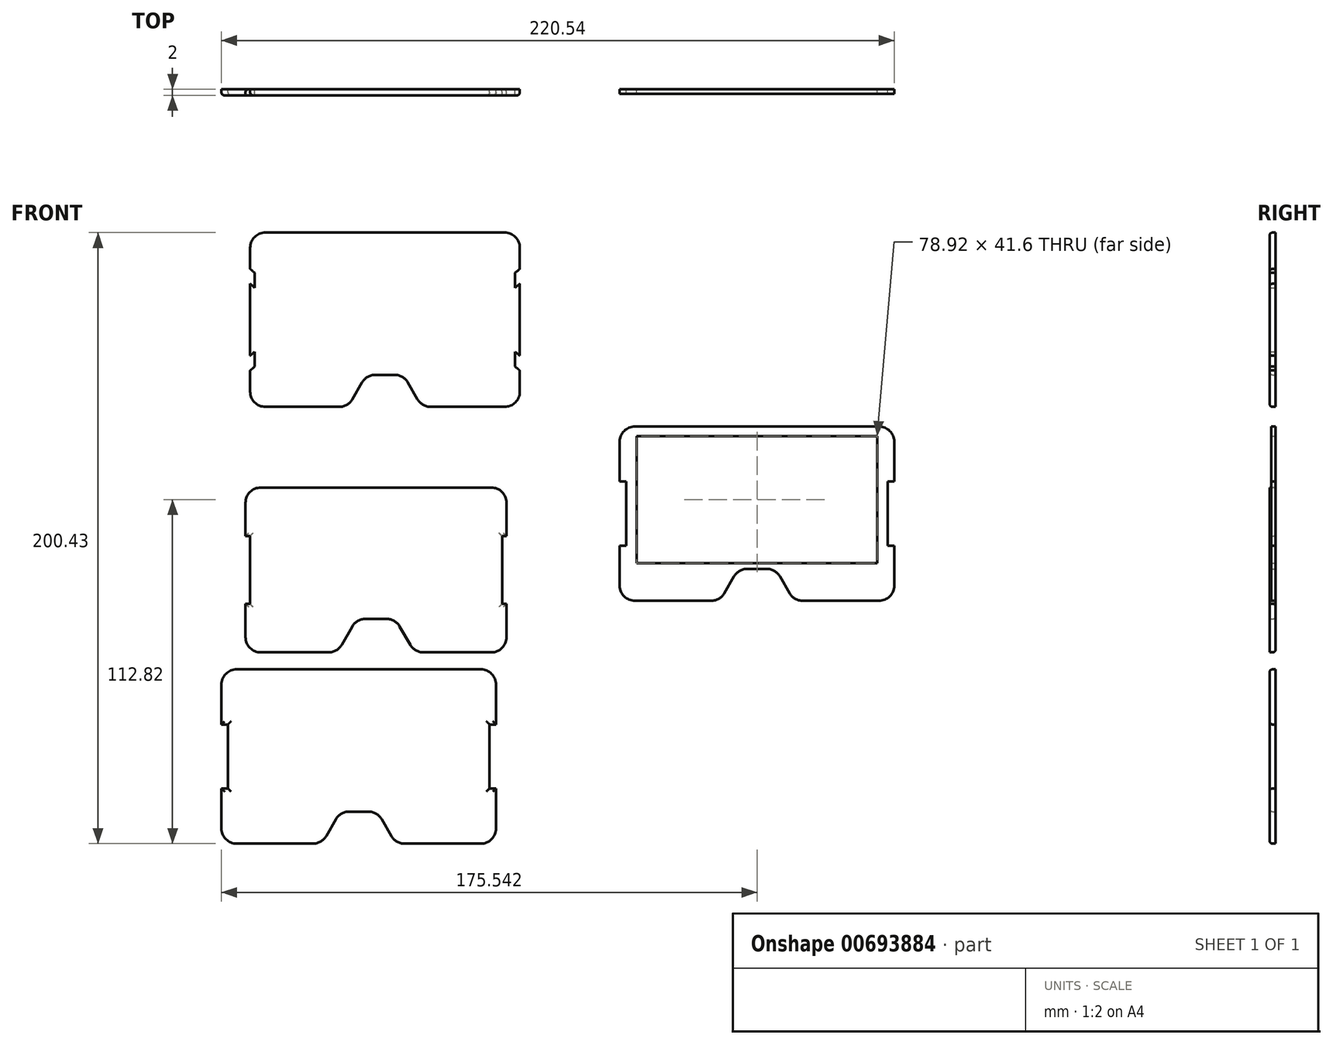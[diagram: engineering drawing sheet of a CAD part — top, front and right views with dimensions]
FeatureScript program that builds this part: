
annotation { "Feature Type Name" : "Feature", "Feature Type Description" : "" }
export const myFeature = defineFeature(function(context is Context, id is Id, definition is map)
    precondition{}
    {
        {
            var Q0;
            Q0=qCreatedBy(makeId("Front.planeOp"),FACE);
            var sketch = newSketch(context, id + "F0", { "sketchPlane" : qUnion([Q0])});
            skPoint(sketch, "E0.middle", {"position": v(0, 0) * mm});
            skPoint(sketch, "E1.visualSharp", {"position": v(43.77, 28.02) * mm});
            skArc(sketch, "E1.filletArc", {"start": v(42.78, 22.03) * mm, "mid": v(41.32, 25.56) * mm, "end": v(37.78, 27.03) * mm});
            skPoint(sketch, "E2.visualSharp", {"position": v(-42.78, 27.03) * mm});
            skArc(sketch, "E2.filletArc", {"start": v(-37.78, 27.03) * mm, "mid": v(-41.32, 25.56) * mm, "end": v(-42.78, 22.03) * mm});
            skPoint(sketch, "E3.visualSharp", {"position": v(-43.77, -28.02) * mm});
            skArc(sketch, "E3.filletArc", {"start": v(-42.78, -22.03) * mm, "mid": v(-41.32, -25.56) * mm, "end": v(-37.78, -27.03) * mm});
            skPoint(sketch, "E4.visualSharp", {"position": v(42.78, -27.03) * mm});
            skArc(sketch, "E4.filletArc", {"start": v(37.78, -27.03) * mm, "mid": v(41.32, -25.56) * mm, "end": v(42.78, -22.03) * mm});
            skLineSegment(sketch, "E5", {"start": v(42.78, 0) * mm, "end": v(0, 0) * mm, "construction": true});
            skLineSegment(sketch, "E6", {"start": v(0, 0) * mm, "end": v(0, 27.03) * mm, "construction": true});
            skLineSegment(sketch, "E7", {"start": v(42.78, 13.02) * mm, "end": v(42.78, 22.03) * mm});
            skLineSegment(sketch, "E8.2", {"start": v(-11.23, -24.53) * mm, "end": v(-7.78, -18.55) * mm});
            skLineSegment(sketch, "E8.3", {"start": v(-3.45, -16.05) * mm, "end": v(3.45, -16.05) * mm});
            skLineSegment(sketch, "E8.4", {"start": v(7.78, -18.55) * mm, "end": v(11.23, -24.53) * mm});
            skPoint(sketch, "E8.0.midPoint", {"position": v(0, -38) * mm});
            skLineSegment(sketch, "E9", {"start": v(37.78, -27.03) * mm, "end": v(15.56, -27.03) * mm});
            skLineSegment(sketch, "E10", {"start": v(-15.56, -27.03) * mm, "end": v(-37.78, -27.03) * mm});
            skLineSegment(sketch, "E11", {"start": v(-37.78, 27.03) * mm, "end": v(37.78, 27.03) * mm});
            skPoint(sketch, "E12.visualSharp", {"position": v(12.67, -27.03) * mm});
            skArc(sketch, "E12.filletArc", {"start": v(11.23, -24.53) * mm, "mid": v(13.06, -26.36) * mm, "end": v(15.56, -27.03) * mm});
            skPoint(sketch, "E13.visualSharp", {"position": v(6.34, -16.05) * mm});
            skArc(sketch, "E13.filletArc", {"start": v(7.78, -18.55) * mm, "mid": v(5.95, -16.72) * mm, "end": v(3.45, -16.05) * mm});
            skPoint(sketch, "E14.visualSharp", {"position": v(-6.34, -16.05) * mm});
            skArc(sketch, "E14.filletArc", {"start": v(-3.45, -16.05) * mm, "mid": v(-5.95, -16.72) * mm, "end": v(-7.78, -18.55) * mm});
            skPoint(sketch, "E15.visualSharp", {"position": v(-12.67, -27.03) * mm});
            skArc(sketch, "E15.filletArc", {"start": v(-15.56, -27.03) * mm, "mid": v(-13.06, -26.36) * mm, "end": v(-11.23, -24.53) * mm});
            skLineSegment(sketch, "E16", {"start": v(41.35, 0) * mm, "end": v(41.35, 11.08) * mm});
            skLineSegment(sketch, "E17", {"start": v(41.35, 11.08) * mm, "end": v(42.78, 11.08) * mm});
            skLineSegment(sketch, "E18", {"start": v(42.78, 11.08) * mm, "end": v(42.78, 13.02) * mm});
            skLineSegment(sketch, "E19.MirrorCS", {"start": v(41.35, 0) * mm, "end": v(41.35, -11.08) * mm});
            skLineSegment(sketch, "E20.MirrorCS", {"start": v(41.35, -11.08) * mm, "end": v(42.78, -11.08) * mm});
            skLineSegment(sketch, "E21", {"start": v(42.78, -11.08) * mm, "end": v(42.78, -22.03) * mm});
            skLineSegment(sketch, "E22.MirrorCS", {"start": v(-41.35, 0) * mm, "end": v(-41.35, -11.08) * mm});
            skLineSegment(sketch, "E23.MirrorCS", {"start": v(-41.35, -11.08) * mm, "end": v(-42.78, -11.08) * mm});
            skLineSegment(sketch, "E24.MirrorCS", {"start": v(-41.35, 11.08) * mm, "end": v(-42.78, 11.08) * mm});
            skLineSegment(sketch, "E25.MirrorCS", {"start": v(-41.35, 0) * mm, "end": v(-41.35, 11.08) * mm});
            skLineSegment(sketch, "E26", {"start": v(-42.78, 22.03) * mm, "end": v(-42.78, 11.08) * mm});
            skLineSegment(sketch, "E27", {"start": v(-42.78, -22.03) * mm, "end": v(-42.78, -11.08) * mm});
            skSolve(sketch);
        }
        {
            var Q0;
            Q0=makeQuery(id+"F0.imprint","IMPRINT",FACE,{"disambiguationData":[TD([[makeQuery(id+"F0.imprint","IMPRINT",EDGE,{"derivedFrom":sQuery(id+"F0.wireOp",EDGE,"E1.filletArc")}),1.0]])]});
            extrude(context, id + "F1", {"entities" : qUnion([Q0]), "depth" : 2 * mm, "offsetDistance" : 25 * mm});
        }
        {
            var Q0;
            Q0=makeQuery(id+"F1.opExtrude","CAP_FACE",FACE,{"disambiguationData":[OSD([sQuery(id+"F0.wireOp",EDGE,"E1.filletArc"),sQuery(id+"F0.wireOp",EDGE,"E2.filletArc"),sQuery(id+"F0.wireOp",EDGE,"E3.filletArc"),sQuery(id+"F0.wireOp",EDGE,"E4.filletArc"),sQuery(id+"F0.wireOp",EDGE,"swWxlsA6-b0p4-RpLw-KjBK-F9TTlwRh0JCC.bottom"),sQuery(id+"F0.wireOp",EDGE,"swWxlsA6-b0p4-RpLw-KjBK-F9TTlwRh0JCC.top"),sQuery(id+"F0.wireOp",EDGE,"swWxlsA6-b0p4-RpLw-KjBK-F9TTlwRh0JCC.right"),sQuery(id+"F0.wireOp",EDGE,"38b65e96-5360-40c4-b25c-9e81677ce4790.MirrorCS"),sQuery(id+"F0.wireOp",EDGE,"38b65e96-5360-40c4-b25c-9e81677ce4791.MirrorCS"),sQuery(id+"F0.wireOp",EDGE,"38b65e96-5360-40c4-b25c-9e81677ce4792.MirrorCS"),sQuery(id+"F0.wireOp",EDGE,"1M21Hp1W-tZvE-ZjFn-AURu-wiaH579pFp8t"),sQuery(id+"F0.wireOp",EDGE,"E7"),sQuery(id+"F0.wireOp",EDGE,"a8fVo7L8-jyON-3xXB-mA3J-mLnhyzgucnCO"),sQuery(id+"F0.wireOp",EDGE,"VKjqsVk1-CC2T-ZNqS-4vh9-m0KNvKaINnyJ"),sQuery(id+"F0.wireOp",EDGE,"E8.2"),sQuery(id+"F0.wireOp",EDGE,"E8.3"),sQuery(id+"F0.wireOp",EDGE,"E8.4"),sQuery(id+"F0.wireOp",EDGE,"E9"),sQuery(id+"F0.wireOp",EDGE,"E10"),sQuery(id+"F0.wireOp",EDGE,"E11"),sQuery(id+"F0.wireOp",EDGE,"E12.filletArc"),sQuery(id+"F0.wireOp",EDGE,"E13.filletArc"),sQuery(id+"F0.wireOp",EDGE,"E14.filletArc"),sQuery(id+"F0.wireOp",EDGE,"E15.filletArc")])],"isStart":true});
            fillet(context, id + "F2", {"entities" : qUnion([Q0]), "radius" : 1 * mm, "tangentPropagation" : true, "allowEdgeOverflow" : false});
        }
        {
            var Q0;
            Q0=qCreatedBy(makeId("Front.planeOp"),FACE);
            var sketch = newSketch(context, id + "F3", { "sketchPlane" : qUnion([Q0])});
            skLineSegment(sketch, "E28.bottom", {"start": v(-45.66, -32.6) * mm, "end": v(34.34, -32.6) * mm});
            skLineSegment(sketch, "E29", {"start": v(-5.66, -32.6) * mm, "end": v(-5.66, -89.77) * mm, "construction": true});
            skPoint(sketch, "E30.middle", {"position": v(-5.66, -61.18) * mm});
            skLineSegment(sketch, "E31", {"start": v(-48.54, -61.18) * mm, "end": v(-48.54, -71.68) * mm});
            skLineSegment(sketch, "E32.MirrorCS", {"start": v(-48.54, -61.18) * mm, "end": v(-48.54, -50.68) * mm});
            skLineSegment(sketch, "E33", {"start": v(-48.54, -50.68) * mm, "end": v(-50.66, -50.68) * mm});
            skLineSegment(sketch, "E34", {"start": v(-48.54, -71.68) * mm, "end": v(-50.66, -71.68) * mm});
            skLineSegment(sketch, "E35", {"start": v(-50.66, -84.77) * mm, "end": v(-50.66, -71.68) * mm});
            skLineSegment(sketch, "E36", {"start": v(-50.66, -50.68) * mm, "end": v(-50.66, -37.6) * mm});
            skLineSegment(sketch, "E37", {"start": v(-5.66, -61.18) * mm, "end": v(-48.54, -61.18) * mm, "construction": true});
            skLineSegment(sketch, "E38.MirrorCS", {"start": v(37.22, -71.68) * mm, "end": v(39.34, -71.68) * mm});
            skLineSegment(sketch, "E39.MirrorCS", {"start": v(37.22, -61.18) * mm, "end": v(37.22, -71.68) * mm});
            skLineSegment(sketch, "E40.MirrorCS", {"start": v(37.22, -61.18) * mm, "end": v(37.22, -50.68) * mm});
            skLineSegment(sketch, "E41.MirrorCS", {"start": v(37.22, -50.68) * mm, "end": v(39.34, -50.68) * mm});
            skLineSegment(sketch, "E42", {"start": v(39.34, -37.6) * mm, "end": v(39.34, -50.68) * mm});
            skLineSegment(sketch, "E43", {"start": v(39.34, -71.68) * mm, "end": v(39.34, -84.77) * mm});
            skLineSegment(sketch, "E44.0", {"start": v(-8.84, -79.26) * mm, "end": v(-2.48, -79.26) * mm});
            skLineSegment(sketch, "E44.1", {"start": v(1.85, -81.76) * mm, "end": v(5.02, -87.27) * mm});
            skLineSegment(sketch, "E44.5", {"start": v(-16.34, -87.27) * mm, "end": v(-13.17, -81.76) * mm});
            skPoint(sketch, "E44.0.midPoint", {"position": v(-5.66, -79.26) * mm});
            skLineSegment(sketch, "E45", {"start": v(-45.66, -89.77) * mm, "end": v(-20.67, -89.77) * mm});
            skLineSegment(sketch, "E46", {"start": v(9.35, -89.77) * mm, "end": v(34.34, -89.77) * mm});
            skPoint(sketch, "E47.visualSharp", {"position": v(-50.66, -32.6) * mm});
            skArc(sketch, "E47.filletArc", {"start": v(-45.66, -32.6) * mm, "mid": v(-49.2, -34.06) * mm, "end": v(-50.66, -37.6) * mm});
            skPoint(sketch, "E48.visualSharp", {"position": v(39.34, -32.6) * mm});
            skArc(sketch, "E48.filletArc", {"start": v(39.34, -37.6) * mm, "mid": v(37.88, -34.06) * mm, "end": v(34.34, -32.6) * mm});
            skPoint(sketch, "E49.visualSharp", {"position": v(39.34, -89.77) * mm});
            skArc(sketch, "E49.filletArc", {"start": v(34.34, -89.77) * mm, "mid": v(37.88, -88.3) * mm, "end": v(39.34, -84.77) * mm});
            skPoint(sketch, "E50.visualSharp", {"position": v(6.47, -89.77) * mm});
            skArc(sketch, "E50.filletArc", {"start": v(5.02, -87.27) * mm, "mid": v(6.85, -89.1) * mm, "end": v(9.35, -89.77) * mm});
            skPoint(sketch, "E51.visualSharp", {"position": v(0.4, -79.26) * mm});
            skArc(sketch, "E51.filletArc", {"start": v(1.85, -81.76) * mm, "mid": v(0.02, -79.93) * mm, "end": v(-2.48, -79.26) * mm});
            skPoint(sketch, "E52.visualSharp", {"position": v(-11.72, -79.26) * mm});
            skArc(sketch, "E52.filletArc", {"start": v(-8.84, -79.26) * mm, "mid": v(-11.34, -79.93) * mm, "end": v(-13.17, -81.76) * mm});
            skPoint(sketch, "E53.visualSharp", {"position": v(-17.79, -89.77) * mm});
            skArc(sketch, "E53.filletArc", {"start": v(-20.67, -89.77) * mm, "mid": v(-18.17, -89.1) * mm, "end": v(-16.34, -87.27) * mm});
            skPoint(sketch, "E54.visualSharp", {"position": v(-50.66, -89.77) * mm});
            skArc(sketch, "E54.filletArc", {"start": v(-50.66, -84.77) * mm, "mid": v(-49.2, -88.3) * mm, "end": v(-45.66, -89.77) * mm});
            skSolve(sketch);
        }
        {
            var Q0;
            Q0=makeQuery(id+"F3.imprint","IMPRINT",FACE,{"disambiguationData":[TD([[makeQuery(id+"F3.imprint","IMPRINT",EDGE,{"derivedFrom":sQuery(id+"F3.wireOp",EDGE,"E28.bottom")}),-1.0]])]});
            extrude(context, id + "F4", {"entities" : qUnion([Q0]), "depth" : 2 * mm, "offsetDistance" : 25 * mm});
        }
        {
            var Q0;
            Q0=makeQuery(id+"F4.opExtrude","CAP_FACE",FACE,{"disambiguationData":[OSD([sQuery(id+"F3.wireOp",EDGE,"E28.bottom"),sQuery(id+"F3.wireOp",EDGE,"E31"),sQuery(id+"F3.wireOp",EDGE,"E32.MirrorCS"),sQuery(id+"F3.wireOp",EDGE,"E33"),sQuery(id+"F3.wireOp",EDGE,"E34"),sQuery(id+"F3.wireOp",EDGE,"E35"),sQuery(id+"F3.wireOp",EDGE,"E36"),sQuery(id+"F3.wireOp",EDGE,"E38.MirrorCS"),sQuery(id+"F3.wireOp",EDGE,"E39.MirrorCS"),sQuery(id+"F3.wireOp",EDGE,"E40.MirrorCS"),sQuery(id+"F3.wireOp",EDGE,"E41.MirrorCS"),sQuery(id+"F3.wireOp",EDGE,"E42"),sQuery(id+"F3.wireOp",EDGE,"E43"),sQuery(id+"F3.wireOp",EDGE,"E44.0"),sQuery(id+"F3.wireOp",EDGE,"E44.1"),sQuery(id+"F3.wireOp",EDGE,"E44.5"),sQuery(id+"F3.wireOp",EDGE,"E45"),sQuery(id+"F3.wireOp",EDGE,"E46"),sQuery(id+"F3.wireOp",EDGE,"E47.filletArc"),sQuery(id+"F3.wireOp",EDGE,"E48.filletArc"),sQuery(id+"F3.wireOp",EDGE,"E49.filletArc"),sQuery(id+"F3.wireOp",EDGE,"E50.filletArc"),sQuery(id+"F3.wireOp",EDGE,"E51.filletArc"),sQuery(id+"F3.wireOp",EDGE,"E52.filletArc"),sQuery(id+"F3.wireOp",EDGE,"E53.filletArc"),sQuery(id+"F3.wireOp",EDGE,"E54.filletArc")])],"isStart":false});
            fillet(context, id + "F5", {"entities" : qUnion([Q0]), "radius" : 1 * mm, "tangentPropagation" : true, "allowEdgeOverflow" : false});
        }
        {
            var Q0;
            Q0=qCreatedBy(makeId("Front.planeOp"),FACE);
            var sketch = newSketch(context, id + "F6", { "sketchPlane" : qUnion([Q0])});
            skLineSegment(sketch, "E55", {"start": v(2.94, 110.66) * mm, "end": v(2.94, 53.5) * mm, "construction": true});
            skPoint(sketch, "E56.middle", {"position": v(2.94, 82.08) * mm});
            skPoint(sketch, "E57.0.midPoint", {"position": v(2.94, 64) * mm});
            skLineSegment(sketch, "E58.MirrorCS", {"start": v(-0.24, 64) * mm, "end": v(2.94, 64) * mm});
            skLineSegment(sketch, "E59.MirrorCS", {"start": v(-39.74, 71.58) * mm, "end": v(-41.26, 70.28) * mm});
            skLineSegment(sketch, "E60.MirrorCS", {"start": v(-39.74, 92.58) * mm, "end": v(-41.26, 93.88) * mm});
            skPoint(sketch, "E61.MirrorP", {"position": v(-9.19, 53.5) * mm});
            skLineSegment(sketch, "E62.MirrorCS", {"start": v(-41.26, 93.88) * mm, "end": v(-41.26, 82.08) * mm});
            skLineSegment(sketch, "E63.MirrorCS", {"start": v(-39.74, 82.08) * mm, "end": v(-39.74, 71.58) * mm});
            skLineSegment(sketch, "E64.MirrorCS", {"start": v(-4.57, 61.5) * mm, "end": v(-7.74, 56) * mm});
            skArc(sketch, "E65.MirrorCS", {"start": v(-7.74, 56) * mm, "mid": v(-9.57, 54.16) * mm, "end": v(-12.07, 53.5) * mm});
            skLineSegment(sketch, "E66.MirrorCS", {"start": v(-39.74, 82.08) * mm, "end": v(-39.74, 92.58) * mm});
            skArc(sketch, "E67.MirrorCS", {"start": v(-4.57, 61.5) * mm, "mid": v(-2.74, 63.33) * mm, "end": v(-0.24, 64) * mm});
            skLineSegment(sketch, "E68.MirrorCS", {"start": v(-41.26, 70.28) * mm, "end": v(-41.26, 82.08) * mm});
            skPoint(sketch, "E69.MirrorP", {"position": v(-3.12, 64) * mm});
            skPoint(sketch, "E70.visualSharp", {"position": v(-39.74, 53.5) * mm});
            skLineSegment(sketch, "E71", {"start": v(-36.26, 110.66) * mm, "end": v(2.94, 110.66) * mm});
            skPoint(sketch, "E72.visualSharp", {"position": v(-41.26, 110.66) * mm});
            skArc(sketch, "E72.filletArc", {"start": v(-36.26, 110.66) * mm, "mid": v(-39.8, 109.2) * mm, "end": v(-41.26, 105.66) * mm});
            skLineSegment(sketch, "E73", {"start": v(-39.74, 82.08) * mm, "end": v(2.94, 82.08) * mm, "construction": true});
            skLineSegment(sketch, "E74.MirrorCS", {"start": v(-39.74, 71.58) * mm, "end": v(-39.74, 66.72) * mm});
            skArc(sketch, "E75.MirrorCS", {"start": v(-36.26, 53.5) * mm, "mid": v(-39.8, 54.96) * mm, "end": v(-41.26, 58.5) * mm});
            skLineSegment(sketch, "E76", {"start": v(-36.26, 53.5) * mm, "end": v(-12.07, 53.5) * mm});
            skLineSegment(sketch, "E77.MirrorCS", {"start": v(42.14, 110.66) * mm, "end": v(2.94, 110.66) * mm});
            skLineSegment(sketch, "E78.MirrorCS", {"start": v(6.12, 64) * mm, "end": v(2.94, 64) * mm});
            skArc(sketch, "E79.MirrorCS", {"start": v(42.14, 110.66) * mm, "mid": v(45.67, 109.2) * mm, "end": v(47.14, 105.66) * mm});
            skLineSegment(sketch, "E80.MirrorCS", {"start": v(45.62, 82.08) * mm, "end": v(45.62, 71.58) * mm});
            skPoint(sketch, "E81.MirrorP", {"position": v(15.07, 53.5) * mm});
            skPoint(sketch, "E82.MirrorP", {"position": v(45.62, 53.5) * mm});
            skLineSegment(sketch, "E83.MirrorCS", {"start": v(10.45, 61.5) * mm, "end": v(13.62, 56) * mm});
            skArc(sketch, "E84.MirrorCS", {"start": v(13.62, 56) * mm, "mid": v(15.45, 54.16) * mm, "end": v(17.95, 53.5) * mm});
            skPoint(sketch, "E85.MirrorP", {"position": v(47.14, 110.66) * mm});
            skLineSegment(sketch, "E86.MirrorCS", {"start": v(45.62, 92.58) * mm, "end": v(47.14, 93.88) * mm});
            skLineSegment(sketch, "E87.MirrorCS", {"start": v(47.14, 93.88) * mm, "end": v(47.14, 82.08) * mm});
            skArc(sketch, "E88.MirrorCS", {"start": v(10.45, 61.5) * mm, "mid": v(8.62, 63.33) * mm, "end": v(6.12, 64) * mm});
            skArc(sketch, "E89.MirrorCS", {"start": v(42.14, 53.5) * mm, "mid": v(45.67, 54.96) * mm, "end": v(47.14, 58.5) * mm});
            skLineSegment(sketch, "E90.MirrorCS", {"start": v(45.62, 71.58) * mm, "end": v(47.14, 70.28) * mm});
            skLineSegment(sketch, "E91.MirrorCS", {"start": v(42.14, 53.5) * mm, "end": v(17.95, 53.5) * mm});
            skLineSegment(sketch, "E92.MirrorCS", {"start": v(45.62, 92.58) * mm, "end": v(45.62, 97.43) * mm});
            skPoint(sketch, "E93.MirrorP", {"position": v(9, 64) * mm});
            skLineSegment(sketch, "E94.MirrorCS", {"start": v(45.62, 82.08) * mm, "end": v(45.62, 92.58) * mm});
            skLineSegment(sketch, "E95.MirrorCS", {"start": v(45.62, 71.58) * mm, "end": v(45.62, 66.72) * mm});
            skLineSegment(sketch, "E96.MirrorCS", {"start": v(47.14, 70.28) * mm, "end": v(47.14, 82.08) * mm});
            skLineSegment(sketch, "E97.MirrorCS", {"start": v(-41.26, 65.43) * mm, "end": v(-39.74, 66.72) * mm});
            skLineSegment(sketch, "E98", {"start": v(-41.26, 65.43) * mm, "end": v(-41.26, 58.5) * mm});
            skLineSegment(sketch, "E99.MirrorCS", {"start": v(-41.26, 98.73) * mm, "end": v(-41.26, 105.66) * mm});
            skLineSegment(sketch, "E100.MirrorCS", {"start": v(-39.74, 92.58) * mm, "end": v(-39.74, 97.43) * mm});
            skLineSegment(sketch, "E101.MirrorCS", {"start": v(-41.26, 98.73) * mm, "end": v(-39.74, 97.43) * mm});
            skLineSegment(sketch, "E102.MirrorCS", {"start": v(47.14, 65.43) * mm, "end": v(47.14, 58.5) * mm});
            skLineSegment(sketch, "E103.MirrorCS", {"start": v(47.14, 65.43) * mm, "end": v(45.62, 66.72) * mm});
            skLineSegment(sketch, "E104.MirrorCS", {"start": v(47.14, 98.73) * mm, "end": v(45.62, 97.43) * mm});
            skLineSegment(sketch, "E105.MirrorCS", {"start": v(47.14, 98.73) * mm, "end": v(47.14, 105.66) * mm});
            skLineSegment(sketch, "E106.bottom", {"start": v(-39.74, 92.58) * mm, "end": v(45.62, 92.58) * mm});
            skLineSegment(sketch, "E106.top", {"start": v(-39.74, 71.58) * mm, "end": v(45.62, 71.58) * mm});
            skLineSegment(sketch, "E106.left", {"start": v(-39.74, 92.58) * mm, "end": v(-39.74, 71.58) * mm});
            skLineSegment(sketch, "E106.right", {"start": v(45.62, 92.58) * mm, "end": v(45.62, 71.58) * mm});
            skSolve(sketch);
        }
        {
            var Q0;
            Q0=makeQuery(id+"F6.imprint","IMPRINT",FACE,{"disambiguationData":[TD([[makeQuery(id+"F6.imprint","IMPRINT",EDGE,{"derivedFrom":sQuery(id+"F6.wireOp",EDGE,"E106.bottom")}),-1.0]])]});
            var Q1;
            Q1=makeQuery(id+"F6.imprint","IMPRINT",FACE,{"disambiguationData":[TD([[makeQuery(id+"F6.imprint","IMPRINT",EDGE,{"derivedFrom":sQuery(id+"F6.wireOp",EDGE,"E71")}),-1.0]])]});
            var Q2;
            Q2=makeQuery(id+"F6.imprint","IMPRINT",FACE,{"disambiguationData":[TD([[makeQuery(id+"F6.imprint","IMPRINT",EDGE,{"derivedFrom":sQuery(id+"F6.wireOp",EDGE,"E59.MirrorCS")}),-1.0]])]});
            var Q3;
            Q3=makeQuery(id+"F6.imprint","IMPRINT",FACE,{"disambiguationData":[TD([[makeQuery(id+"F6.imprint","IMPRINT",EDGE,{"derivedFrom":sQuery(id+"F6.wireOp",EDGE,"E58.MirrorCS")}),1.0]])]});
            var Q4;
            Q4=makeQuery(id+"F6.imprint","IMPRINT",FACE,{"disambiguationData":[TD([[makeQuery(id+"F6.imprint","IMPRINT",EDGE,{"derivedFrom":sQuery(id+"F6.wireOp",EDGE,"E86.MirrorCS")}),-1.0]])]});
            extrude(context, id + "F7", {"entities" : qUnion([Q0, Q1, Q2, Q3, Q4]), "depth" : 2 * mm, "offsetDistance" : 25 * mm});
        }
        {
            var Q0;
            Q0=makeQuery(id+"F7.opExtrude","CAP_EDGE",EDGE,{"disambiguationData":[OSD([sQuery(id+"F6.wireOp",EDGE,"E72.filletArc")])],"isStart":false});
            var Q1;
            Q1=makeQuery(id+"F7.opExtrude","CAP_EDGE",EDGE,{"disambiguationData":[OSD([sQuery(id+"F6.wireOp",EDGE,"E89.MirrorCS")])],"isStart":false});
            fillet(context, id + "F8", {"entities" : qUnion([Q0, Q1]), "radius" : 1 * mm, "tangentPropagation" : true, "allowEdgeOverflow" : false});
        }
        {
            var Q0;
            Q0=makeQuery(id+"F7.opExtrude","CAP_EDGE",EDGE,{"disambiguationData":[OSD([sQuery(id+"F6.wireOp",EDGE,"E87.MirrorCS"),sQuery(id+"F6.wireOp",EDGE,"E96.MirrorCS")])],"isStart":false});
            var Q1;
            Q1=makeQuery(id+"F7.opExtrude","CAP_EDGE",EDGE,{"disambiguationData":[OSD([sQuery(id+"F6.wireOp",EDGE,"E62.MirrorCS"),sQuery(id+"F6.wireOp",EDGE,"E68.MirrorCS")])],"isStart":false});
            fillet(context, id + "F9", {"entities" : qUnion([Q0, Q1]), "radius" : 1 * mm, "tangentPropagation" : true, "allowEdgeOverflow" : false});
        }
        {
            var Q0;
            Q0=qCreatedBy(makeId("Front.planeOp"),FACE);
            var sketch = newSketch(context, id + "F10", { "sketchPlane" : qUnion([Q0])});
            skLineSegment(sketch, "E107.bottom", {"start": v(84.88, 47.05) * mm, "end": v(164.88, 47.05) * mm});
            skLineSegment(sketch, "E108", {"start": v(124.88, 47.05) * mm, "end": v(124.88, -10.12) * mm, "construction": true});
            skPoint(sketch, "E109.middle", {"position": v(124.88, 23.05) * mm});
            skLineSegment(sketch, "E110", {"start": v(82, 18.46) * mm, "end": v(82, 7.96) * mm});
            skLineSegment(sketch, "E111.MirrorCS", {"start": v(82, 18.46) * mm, "end": v(82, 28.96) * mm});
            skLineSegment(sketch, "E112", {"start": v(82, 28.96) * mm, "end": v(79.88, 28.96) * mm});
            skLineSegment(sketch, "E113", {"start": v(82, 7.96) * mm, "end": v(79.88, 7.96) * mm});
            skLineSegment(sketch, "E114", {"start": v(79.88, -5.12) * mm, "end": v(79.88, 7.96) * mm});
            skLineSegment(sketch, "E115", {"start": v(79.88, 28.96) * mm, "end": v(79.88, 42.05) * mm});
            skLineSegment(sketch, "E116", {"start": v(124.88, 23.05) * mm, "end": v(82, 18.46) * mm, "construction": true});
            skLineSegment(sketch, "E117.MirrorCS", {"start": v(167.76, 7.96) * mm, "end": v(169.88, 7.96) * mm});
            skLineSegment(sketch, "E118.MirrorCS", {"start": v(167.76, 18.46) * mm, "end": v(167.76, 7.96) * mm});
            skLineSegment(sketch, "E119.MirrorCS", {"start": v(167.76, 18.46) * mm, "end": v(167.76, 28.96) * mm});
            skLineSegment(sketch, "E120.MirrorCS", {"start": v(167.76, 28.96) * mm, "end": v(169.88, 28.96) * mm});
            skLineSegment(sketch, "E121", {"start": v(169.88, 42.05) * mm, "end": v(169.88, 28.96) * mm});
            skLineSegment(sketch, "E122", {"start": v(169.88, 7.96) * mm, "end": v(169.88, -5.12) * mm});
            skLineSegment(sketch, "E123.0", {"start": v(121.7, 0.38) * mm, "end": v(128.06, 0.38) * mm});
            skLineSegment(sketch, "E123.1", {"start": v(132.39, -2.12) * mm, "end": v(135.57, -7.62) * mm});
            skLineSegment(sketch, "E123.5", {"start": v(114.2, -7.62) * mm, "end": v(117.37, -2.12) * mm});
            skPoint(sketch, "E123.0.midPoint", {"position": v(124.88, 0.38) * mm});
            skLineSegment(sketch, "E124", {"start": v(84.88, -10.12) * mm, "end": v(109.87, -10.12) * mm});
            skLineSegment(sketch, "E125", {"start": v(139.9, -10.12) * mm, "end": v(164.88, -10.12) * mm});
            skPoint(sketch, "E126.visualSharp", {"position": v(79.88, 47.05) * mm});
            skArc(sketch, "E126.filletArc", {"start": v(84.88, 47.05) * mm, "mid": v(81.35, 45.58) * mm, "end": v(79.88, 42.05) * mm});
            skPoint(sketch, "E127.visualSharp", {"position": v(169.88, 47.05) * mm});
            skArc(sketch, "E127.filletArc", {"start": v(169.88, 42.05) * mm, "mid": v(168.42, 45.58) * mm, "end": v(164.88, 47.05) * mm});
            skPoint(sketch, "E128.visualSharp", {"position": v(169.88, -10.12) * mm});
            skArc(sketch, "E128.filletArc", {"start": v(164.88, -10.12) * mm, "mid": v(168.42, -8.66) * mm, "end": v(169.88, -5.12) * mm});
            skPoint(sketch, "E129.visualSharp", {"position": v(137, -10.12) * mm});
            skArc(sketch, "E129.filletArc", {"start": v(135.57, -7.62) * mm, "mid": v(137.4, -9.45) * mm, "end": v(139.9, -10.12) * mm});
            skPoint(sketch, "E130.visualSharp", {"position": v(130.95, 0.38) * mm});
            skArc(sketch, "E130.filletArc", {"start": v(132.39, -2.12) * mm, "mid": v(130.56, -0.3) * mm, "end": v(128.06, 0.38) * mm});
            skPoint(sketch, "E131.visualSharp", {"position": v(118.82, 0.38) * mm});
            skArc(sketch, "E131.filletArc", {"start": v(121.7, 0.38) * mm, "mid": v(119.2, -0.3) * mm, "end": v(117.37, -2.12) * mm});
            skPoint(sketch, "E132.visualSharp", {"position": v(112.75, -10.12) * mm});
            skArc(sketch, "E132.filletArc", {"start": v(109.87, -10.12) * mm, "mid": v(112.37, -9.45) * mm, "end": v(114.2, -7.62) * mm});
            skPoint(sketch, "E133.visualSharp", {"position": v(79.88, -10.12) * mm});
            skArc(sketch, "E133.filletArc", {"start": v(79.88, -5.12) * mm, "mid": v(81.35, -8.66) * mm, "end": v(84.88, -10.12) * mm});
            skLineSegment(sketch, "E134.bottom", {"start": v(164.34, 2.25) * mm, "end": v(85.42, 2.25) * mm});
            skLineSegment(sketch, "E134.top", {"start": v(164.34, 43.85) * mm, "end": v(85.42, 43.85) * mm});
            skLineSegment(sketch, "E134.left", {"start": v(164.34, 2.25) * mm, "end": v(164.34, 43.85) * mm});
            skLineSegment(sketch, "E134.right", {"start": v(85.42, 2.25) * mm, "end": v(85.42, 43.85) * mm});
            skSolve(sketch);
        }
        {
            var Q0;
            Q0 = qSketchRegion(id + "F10", true);
            extrude(context, id + "F11", {"entities" : qUnion([Q0]), "depth" : 1.5 * mm, "offsetDistance" : 25 * mm});
        }
    });
